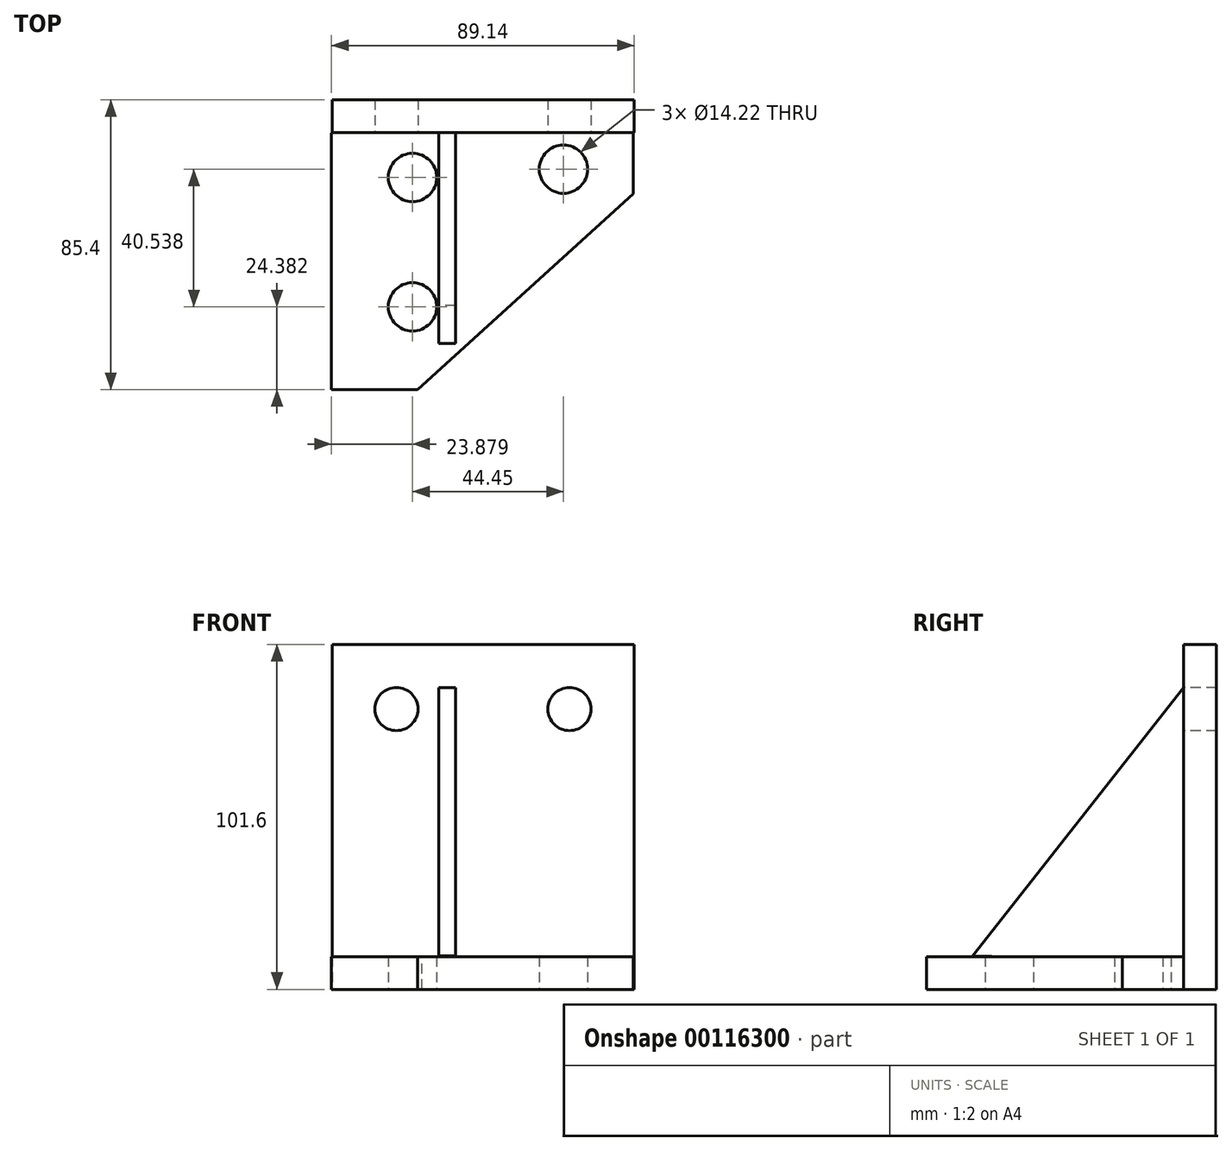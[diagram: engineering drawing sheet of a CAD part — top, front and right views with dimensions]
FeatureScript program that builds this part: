
annotation { "Feature Type Name" : "Feature", "Feature Type Description" : "" }
export const myFeature = defineFeature(function(context is Context, id is Id, definition is map)
    precondition{}
    {
        {
            var Q0;
            Q0=qCreatedBy(makeId("Top.planeOp"),FACE);
            var sketch = newSketch(context, id + "F0", { "sketchPlane" : qUnion([Q0])});
            skLineSegment(sketch, "E0", {"start": v(-34.08, 33.68) * mm, "end": v(-34.08, -41.87) * mm});
            skLineSegment(sketch, "E1", {"start": v(-34.08, -41.87) * mm, "end": v(-8.68, -41.87) * mm});
            skLineSegment(sketch, "E2", {"start": v(-8.68, -41.87) * mm, "end": v(54.82, 15.77) * mm});
            skLineSegment(sketch, "E3", {"start": v(54.82, 15.77) * mm, "end": v(54.82, 34.33) * mm});
            skLineSegment(sketch, "E4", {"start": v(54.82, 34.33) * mm, "end": v(-34.08, 33.68) * mm});
            skCircle(sketch, "E5", {"center": v(34.25, 23.05) * mm, "radius": 7.11 * mm});
            skCircle(sketch, "E6", {"center": v(-10.2, 20.61) * mm, "radius": 7.11 * mm});
            skCircle(sketch, "E7", {"center": v(-10.2, -17.49) * mm, "radius": 7.11 * mm});
            skSolve(sketch);
        }
        {
            var Q0;
            Q0 = qSketchRegion(id + "F0", true);
            extrude(context, id + "F1", {"entities" : qUnion([Q0]), "depth" : 9.65 * mm});
        }
        {
            var Q0;
            Q0=qCreatedBy(makeId("Right.planeOp"),FACE);
            var sketch = newSketch(context, id + "F2", { "sketchPlane" : qUnion([Q0])});
            skLineSegment(sketch, "E8", {"start": v(33.88, 88.9) * mm, "end": v(-28.2, 9.8) * mm});
            skLineSegment(sketch, "E9", {"start": v(-28.2, 9.8) * mm, "end": v(33.88, 8.95) * mm});
            skLineSegment(sketch, "E10", {"start": v(33.88, 88.9) * mm, "end": v(33.88, 8.95) * mm});
            skSolve(sketch);
        }
        {
            var Q0;
            Q0 = qSketchRegion(id + "F2", true);
            extrude(context, id + "F3", {"entities" : qUnion([Q0]), "operationType" : NewBodyOperationType.ADD, "endBound" : BoundingType.SYMMETRIC, "depth" : 4.95 * mm});
        }
        {
            var Q0;
            Q0=makeQuery(id+"F3.opExtrude","SWEPT_FACE",FACE,{"disambiguationData":[OSD([sQuery(id+"F2.wireOp",EDGE,"E10")])]});
            var sketch = newSketch(context, id + "F4", { "sketchPlane" : qUnion([Q0])});
            skLineSegment(sketch, "E11", {"start": v(-55.06, 0) * mm, "end": v(-55.06, 101.6) * mm});
            skLineSegment(sketch, "E12", {"start": v(33.84, 101.6) * mm, "end": v(33.84, 0) * mm});
            skLineSegment(sketch, "E13", {"start": v(33.84, 0) * mm, "end": v(-55.06, 0) * mm});
            skLineSegment(sketch, "E14", {"start": v(33.84, 101.6) * mm, "end": v(-55.06, 101.6) * mm});
            skCircle(sketch, "E15", {"center": v(-36.01, 82.55) * mm, "radius": 6.35 * mm});
            skCircle(sketch, "E16", {"center": v(14.94, 82.55) * mm, "radius": 6.35 * mm});
            skSolve(sketch);
        }
        {
            var Q0;
            Q0 = qSketchRegion(id + "F4", true);
            extrude(context, id + "F5", {"entities" : qUnion([Q0]), "operationType" : NewBodyOperationType.ADD, "depth" : 9.65 * mm});
        }
    });
